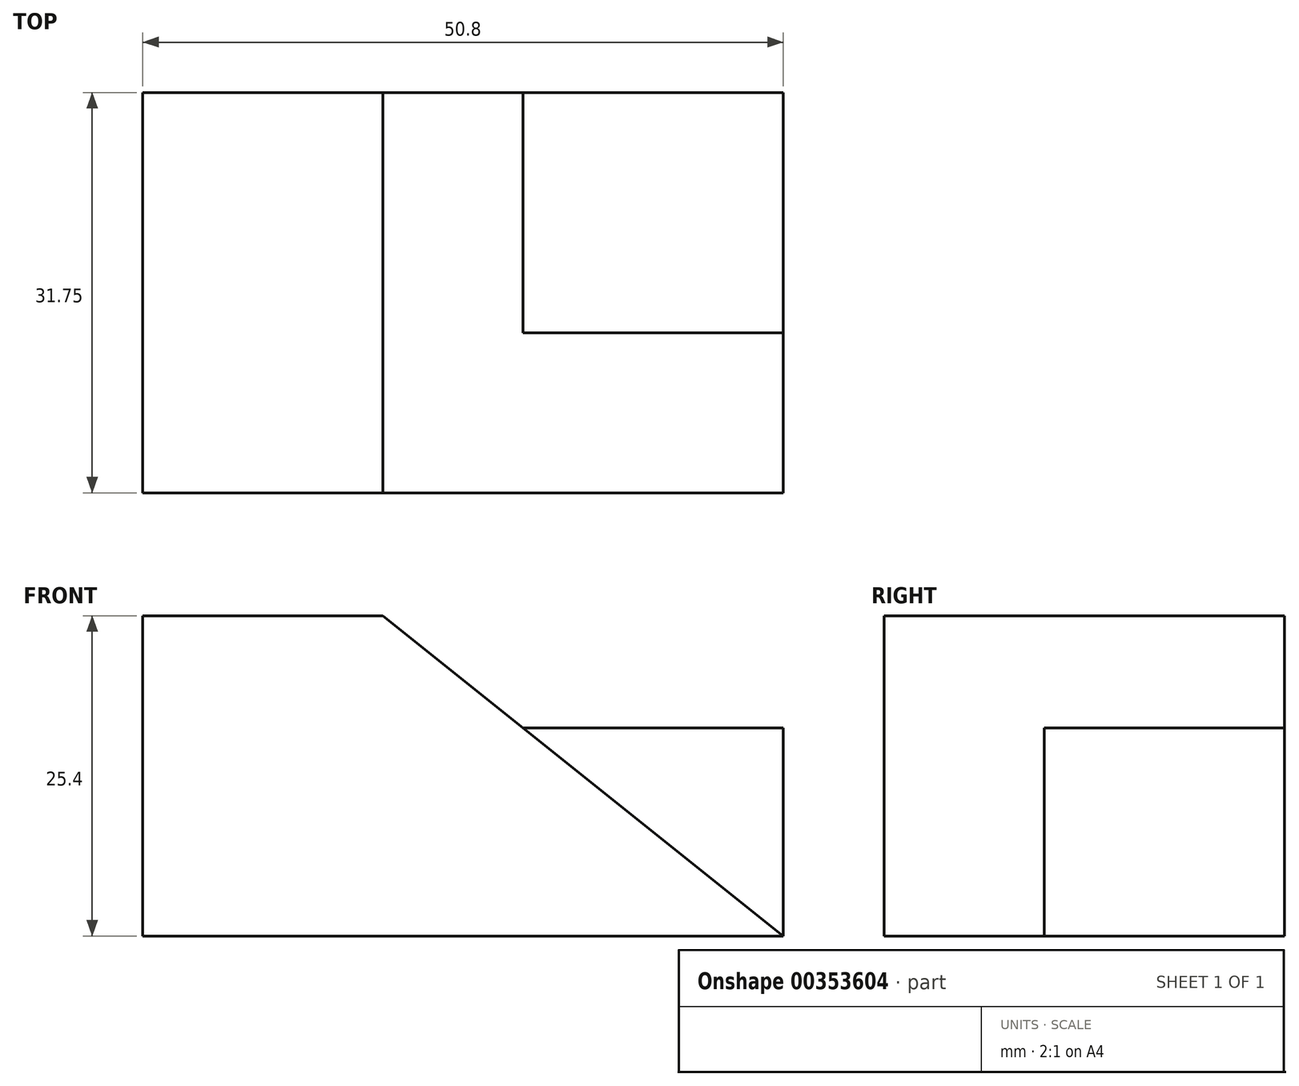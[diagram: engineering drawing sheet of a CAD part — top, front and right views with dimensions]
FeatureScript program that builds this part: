
annotation { "Feature Type Name" : "Feature", "Feature Type Description" : "" }
export const myFeature = defineFeature(function(context is Context, id is Id, definition is map)
    precondition{}
    {
        {
            var Q0;
            Q0=qCreatedBy(makeId("Front.planeOp"),FACE);
            var sketch = newSketch(context, id + "F0", { "sketchPlane" : qUnion([Q0])});
            skLineSegment(sketch, "E0", {"start": v(0, 0) * mm, "end": v(0, 25.4) * mm});
            skLineSegment(sketch, "E1", {"start": v(0, 25.4) * mm, "end": v(50.8, 25.4) * mm});
            skLineSegment(sketch, "E2", {"start": v(50.8, 25.4) * mm, "end": v(50.8, 0) * mm});
            skLineSegment(sketch, "E3", {"start": v(50.8, 0) * mm, "end": v(0, 0) * mm});
            skSolve(sketch);
        }
        {
            var Q0;
            Q0=makeQuery(id+"F0.imprint","IMPRINT",FACE,{"disambiguationData":[TD([[makeQuery(id+"F0.imprint","IMPRINT",EDGE,{"derivedFrom":sQuery(id+"F0.wireOp",EDGE,"E0")}),-1.0]])]});
            extrude(context, id + "F1", {"entities" : qUnion([Q0]), "depth" : 31.75 * mm});
        }
        {
            var Q0;
            Q0=makeQuery(id+"F1.opExtrude","CAP_FACE",FACE,{"disambiguationData":[OSD([sQuery(id+"F0.wireOp",EDGE,"E0"),sQuery(id+"F0.wireOp",EDGE,"E1"),sQuery(id+"F0.wireOp",EDGE,"E2"),sQuery(id+"F0.wireOp",EDGE,"E3")])],"isStart":false});
            var sketch = newSketch(context, id + "F2", { "sketchPlane" : qUnion([Q0])});
            skLineSegment(sketch, "E4", {"start": v(19.05, 25.4) * mm, "end": v(50.8, 0) * mm});
            skLineSegment(sketch, "E5", {"start": v(50.8, 0) * mm, "end": v(50.8, 25.4) * mm});
            skLineSegment(sketch, "E6", {"start": v(50.8, 25.4) * mm, "end": v(19.05, 25.4) * mm});
            skSolve(sketch);
        }
        {
            var Q0;
            Q0=makeQuery(id+"F2.imprint","IMPRINT",FACE,{"disambiguationData":[TD([[makeQuery(id+"F2.imprint","IMPRINT",EDGE,{"derivedFrom":sQuery(id+"F2.wireOp",EDGE,"E4")}),1.0]])]});
            extrude(context, id + "F3", {"entities" : qUnion([Q0]), "operationType" : NewBodyOperationType.REMOVE, "oppositeDirection" : true, "depth" : 31.75 * mm});
        }
        {
            var Q0;
            Q0=makeQuery(id+"F1.opExtrude","CAP_FACE",FACE,{"disambiguationData":[OSD([sQuery(id+"F0.wireOp",EDGE,"E0"),sQuery(id+"F0.wireOp",EDGE,"E1"),sQuery(id+"F0.wireOp",EDGE,"E2"),sQuery(id+"F0.wireOp",EDGE,"E3")])],"isStart":true});
            var sketch = newSketch(context, id + "F4", { "sketchPlane" : qUnion([Q0])});
            skLineSegment(sketch, "E7", {"start": v(-50.8, 0) * mm, "end": v(-50.8, 16.51) * mm});
            skLineSegment(sketch, "E8", {"start": v(-50.8, 16.51) * mm, "end": v(-30.16, 16.51) * mm});
            skLineSegment(sketch, "E9", {"start": v(-30.16, 16.51) * mm, "end": v(-50.8, 0) * mm});
            skSolve(sketch);
        }
        {
            var Q0;
            Q0=makeQuery(id+"F4.imprint","IMPRINT",FACE,{"disambiguationData":[TD([[makeQuery(id+"F4.imprint","IMPRINT",EDGE,{"derivedFrom":sQuery(id+"F4.wireOp",EDGE,"E7")}),-1.0]])]});
            extrude(context, id + "F5", {"entities" : qUnion([Q0]), "operationType" : NewBodyOperationType.ADD, "oppositeDirection" : true, "depth" : 19.05 * mm});
        }
    });
